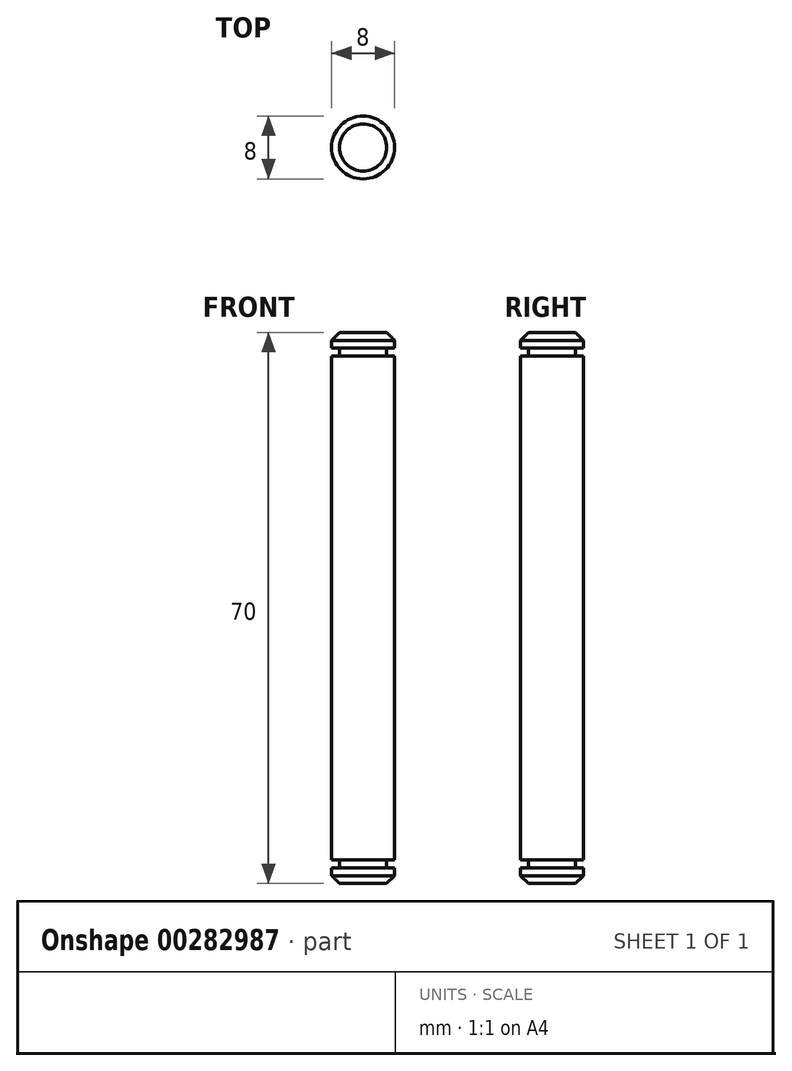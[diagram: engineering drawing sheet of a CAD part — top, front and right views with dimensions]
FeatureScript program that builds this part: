
annotation { "Feature Type Name" : "Feature", "Feature Type Description" : "" }
export const myFeature = defineFeature(function(context is Context, id is Id, definition is map)
    precondition{}
    {
        {
            var Q0;
            Q0=qCreatedBy(makeId("Front.planeOp"),FACE);
            var sketch = newSketch(context, id + "F0", { "sketchPlane" : qUnion([Q0])});
            skLineSegment(sketch, "E0", {"start": v(0, 35) * mm, "end": v(4, 35) * mm});
            skLineSegment(sketch, "E1", {"start": v(4, 35) * mm, "end": v(4, 33) * mm});
            skLineSegment(sketch, "E2", {"start": v(4, 33) * mm, "end": v(3, 33) * mm});
            skLineSegment(sketch, "E3", {"start": v(3, 33) * mm, "end": v(3, 32) * mm});
            skLineSegment(sketch, "E4", {"start": v(3, 32) * mm, "end": v(4, 32) * mm});
            skLineSegment(sketch, "E5", {"start": v(4, 32) * mm, "end": v(4, -32) * mm});
            skLineSegment(sketch, "E6", {"start": v(4, -32) * mm, "end": v(3, -32) * mm});
            skLineSegment(sketch, "E7", {"start": v(3, -32) * mm, "end": v(3, -33) * mm});
            skLineSegment(sketch, "E8", {"start": v(3, -33) * mm, "end": v(4, -33) * mm});
            skLineSegment(sketch, "E9", {"start": v(4, -33) * mm, "end": v(4, -35) * mm});
            skLineSegment(sketch, "E10", {"start": v(4, -35) * mm, "end": v(0, -35) * mm});
            skLineSegment(sketch, "E11", {"start": v(0, 35) * mm, "end": v(0, -35) * mm});
            skLineSegment(sketch, "E12", {"start": v(0, 0) * mm, "end": v(-22.07, 0) * mm, "construction": true});
            skLineSegment(sketch, "E13", {"start": v(0, -35) * mm, "end": v(0, 35) * mm, "construction": true});
            skSolve(sketch);
        }
        {
            var Q0;
            Q0=makeQuery(id+"F0.imprint","IMPRINT",FACE,{"disambiguationData":[TD([[makeQuery(id+"F0.imprint","IMPRINT",EDGE,{"derivedFrom":sQuery(id+"F0.wireOp",EDGE,"E0")}),-1.0]])]});
            var Q1;
            Q1=sQuery(id+"F0.wireOp",EDGE,"E11");
            revolve(context, id + "F1", {"entities" : qUnion([Q0]), "axis" : qUnion([Q1]), "revolveType" : RevolveType.FULL});
        }
        {
            var Q0;
            Q0=makeQuery(id+"F1.opRevolve","SWEPT_EDGE",EDGE,{"disambiguationData":[OSD([sQuery(id+"F0.wireOp",EDGE,"E0"),sQuery(id+"F0.wireOp",EDGE,"E1")])]});
            var Q1;
            Q1=makeQuery(id+"F1.opRevolve","SWEPT_EDGE",EDGE,{"disambiguationData":[OSD([sQuery(id+"F0.wireOp",EDGE,"E9"),sQuery(id+"F0.wireOp",EDGE,"E10")])]});
            chamfer(context, id + "F2", {"entities" : qUnion([Q0, Q1]), "chamferType" : ChamferType.OFFSET_ANGLE, "width" : 1 * mm, "oppositeDirection" : false, "angle" : 45 * degree, "tangentPropagation" : true});
        }
    });
